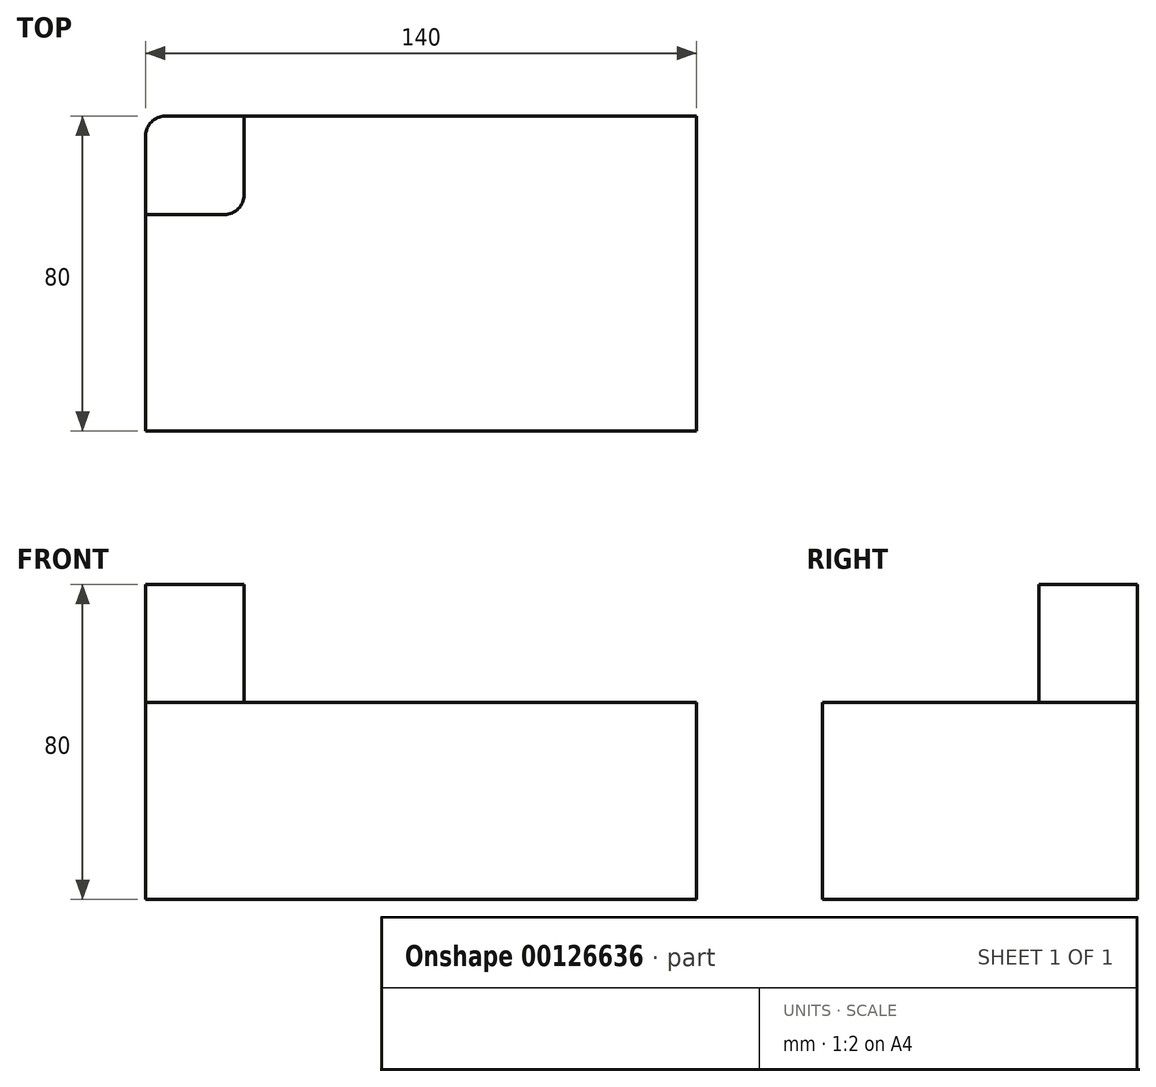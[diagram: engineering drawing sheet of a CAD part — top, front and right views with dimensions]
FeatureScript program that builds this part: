
annotation { "Feature Type Name" : "Feature", "Feature Type Description" : "" }
export const myFeature = defineFeature(function(context is Context, id is Id, definition is map)
    precondition{}
    {
        {
            var Q0;
            Q0=qCreatedBy(makeId("Top.planeOp"),FACE);
            var sketch = newSketch(context, id + "F0", { "sketchPlane" : qUnion([Q0])});
            skLineSegment(sketch, "E0.bottom", {"start": v(-70, 40) * mm, "end": v(70, 40) * mm});
            skLineSegment(sketch, "E0.top", {"start": v(-70, -40) * mm, "end": v(70, -40) * mm});
            skLineSegment(sketch, "E0.left", {"start": v(-70, 40) * mm, "end": v(-70, -40) * mm});
            skLineSegment(sketch, "E0.right", {"start": v(70, 40) * mm, "end": v(70, -40) * mm});
            skLineSegment(sketch, "E1", {"start": v(0, 40) * mm, "end": v(0, 0) * mm});
            skLineSegment(sketch, "E2", {"start": v(0, 0) * mm, "end": v(0, -40) * mm});
            skSolve(sketch);
        }
        {
            var Q0;
            Q0 = qSketchRegion(id + "F0", true);
            extrude(context, id + "F1", {"entities" : qUnion([Q0]), "depth" : 50 * mm});
        }
        {
            var Q0;
            Q0=makeQuery(id+"F1.opExtrude","CAP_FACE",FACE,{"disambiguationData":[OSD([sQuery(id+"F0.wireOp",EDGE,"E0.bottom"),sQuery(id+"F0.wireOp",EDGE,"E0.top"),sQuery(id+"F0.wireOp",EDGE,"E0.left"),sQuery(id+"F0.wireOp",EDGE,"E0.right")])],"isStart":false});
            var sketch = newSketch(context, id + "F2", { "sketchPlane" : qUnion([Q0])});
            skLineSegment(sketch, "E3", {"start": v(-70, 15) * mm, "end": v(-70, 40) * mm});
            skLineSegment(sketch, "E4", {"start": v(-70, 40) * mm, "end": v(-45, 40) * mm});
            skLineSegment(sketch, "E5", {"start": v(-70, 15) * mm, "end": v(-50, 15) * mm});
            skLineSegment(sketch, "E6", {"start": v(-45, 20) * mm, "end": v(-45, 40) * mm});
            skPoint(sketch, "E7.visualSharp", {"position": v(-45, 15) * mm});
            skArc(sketch, "E7.filletArc", {"start": v(-50, 15) * mm, "mid": v(-46.46, 16.46) * mm, "end": v(-45, 20) * mm});
            skSolve(sketch);
        }
        {
            var Q0;
            Q0 = qSketchRegion(id + "F2", true);
            extrude(context, id + "F3", {"entities" : qUnion([Q0]), "operationType" : NewBodyOperationType.ADD, "depth" : 30 * mm});
        }
        {
            var Q0;
            Q0=makeQuery(id+"F3.boolean.opBoolean","MERGE",EDGE,{"derivedFrom":[makeQuery(id+"F1.opExtrude","SWEPT_EDGE",EDGE,{"disambiguationData":[OSD([sQuery(id+"F0.wireOp",EDGE,"E0.bottom"),sQuery(id+"F0.wireOp",EDGE,"E0.left")])]}),makeQuery(id+"F3.opExtrude","SWEPT_EDGE",EDGE,{"disambiguationData":[OSD([sQuery(id+"F2.wireOp",EDGE,"E3"),sQuery(id+"F2.wireOp",EDGE,"E4")])]})]});
            fillet(context, id + "F4", {"entities" : qUnion([Q0]), "radius" : 5 * mm, "tangentPropagation" : true, "allowEdgeOverflow" : false});
        }
    });
